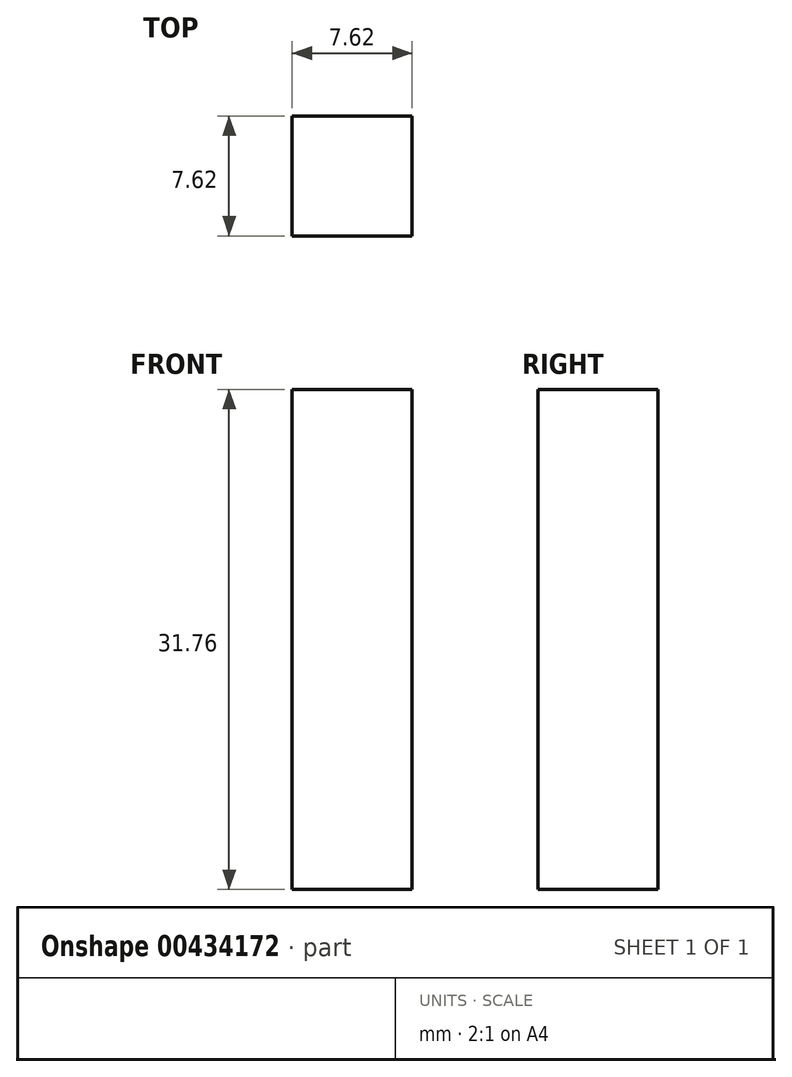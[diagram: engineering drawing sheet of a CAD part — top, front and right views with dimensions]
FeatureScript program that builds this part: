
annotation { "Feature Type Name" : "Feature", "Feature Type Description" : "" }
export const myFeature = defineFeature(function(context is Context, id is Id, definition is map)
    precondition{}
    {
        {
            var Q0;
            Q0=qCreatedBy(makeId("Front.planeOp"),FACE);
            var sketch = newSketch(context, id + "F0", { "sketchPlane" : qUnion([Q0])});
            skLineSegment(sketch, "E0.bottom", {"start": v(-3.81, 15.88) * mm, "end": v(3.8, 15.88) * mm});
            skLineSegment(sketch, "E0.top", {"start": v(-3.8, -15.88) * mm, "end": v(3.81, -15.88) * mm});
            skLineSegment(sketch, "E0.left", {"start": v(-3.81, 15.88) * mm, "end": v(-3.8, -15.88) * mm});
            skLineSegment(sketch, "E0.right", {"start": v(3.8, 15.88) * mm, "end": v(3.81, -15.87) * mm});
            skPoint(sketch, "E0.middle", {"position": v(0, 0) * mm});
            skSolve(sketch);
        }
        {
            var Q0;
            Q0=makeQuery(id+"F0.imprint","IMPRINT",FACE,{"disambiguationData":[TD([[makeQuery(id+"F0.imprint","IMPRINT",EDGE,{"derivedFrom":sQuery(id+"F0.wireOp",EDGE,"E0.bottom")}),-1.0]])]});
            extrude(context, id + "F1", {"entities" : qUnion([Q0]), "depth" : 7.62 * mm});
        }
    });
